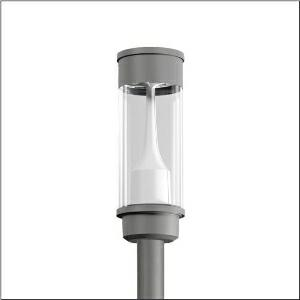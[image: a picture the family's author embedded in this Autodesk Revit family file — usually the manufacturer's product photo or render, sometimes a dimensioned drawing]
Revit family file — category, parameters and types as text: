
# Revit family: litepole_iq___st1_2a_5xa5415af14hp_e371
name_source: partatom
category: Lighting Fixtures
units: mm (PartAtom-declared; Revit-internal decimal feet)

## family parameters
Cut with Voids When Loaded = No
Host = Face
Light Source = No
Part Type = Normal
Room Calculation Point = No
Round Connector Dimension = Use Diameter
Shared = No

## types (1)
- --- (1 x LED, 3910 lm, 33.6 W, 2200K)
    Apparent Load = 34 VA
    CIE Flux Codes = 22 60 93 95 100
    Color Rendering = 70
    Color Temperature = 2200K
    Default Elevation = 1800 mm
    Description = Litepole iQ, mast luminaire, Module 540 iQ-SR, primary light control with 3 zone facetted reflector, of plastic, silver coated, highly specular, structured, primary optical cover: cover, of PMMA, transparent, partly coated, light distribution: ST1.2a, light emission: direct distribution, primary light characteristic: asymmetric, installation type: post-top, LED, High Power LED, rated luminous flux: 3.910lm, luminous efficacy: 116lm/W, light colour: 722, colour temperature: 2200K, control gear: iQ Street-Remote, control: optimised constant luminous flux control (CLO 2.0), Desk-Remote (wireless, voltage-free reading and setting of iQ features in the workshop via application-optimized NFC function/RFID function), Light-Fading, Smart-Wire, Night-Set, Lumen-Switch, Temp-Guard, Auto-Match, Street-Remote, pre-setting: logarithmic dimming characteristic, with terminal, 6-pole, max. 2.5mm², mains connection: 230..240V, AC, 50/60Hz, start of lifetime: 34W, end of service life: 36W, reduction: 15W, luminaire housing, upper part, of glass-fibre reinforced polyester, coated, Siteco® metallic grey (DB 702S), diameter: 210mm, height: 590mm, spigot size: d x l = 76 x 70mm (post-top) | with reducer (optional accessory) 60 x 70mm, mounting height: 3..5m, post-top mast mounting element, of diecast aluminium, coated, Siteco® metallic grey (DB 702S), Module 540 iQ-SR, traffic white (RAL 9016), equipment: Power, protection rating (complete): IP65, insulation class (complete): insulation class II (safety insulation), certification: CE, ENEC, VDE, packaging unit: 1 piece

Light Distribution: ST1.2a
    Height = 590 mm
    Lamp = 1 x LED
    Lamp Light Flux = 3910 lm
    Lamp Power = 33.6 W
    Lamp count = 1
    Length = 220 mm
    Luminous efficacy = 116 lm/W
    Manufacturer = Siteco
    ModVariant = No
    Model = 5XA5415AF14HP
    Number of Poles = 1
    OnlyDefault = Yes
    Power Factor = 1
    Product Name = Litepole iQ | ST1.2a
    Product group = mast luminaire | pylon top
    ProductGroupID = 6100
    Protection Class = Protection class II
    Protection Degree = IP 65
    RLX_Detail_Level = 1
    RLX_Emergency_Light_Flux = 0 lm
    RLX_Emergency_Type = 0
    RLX_Emergency_Type_DB = No
    RlxData = <blob elided: 29725 chars, md5=054f4d41>
    Socket = socket
    Standby Power = 0 W
    System Light Flux = 3910 lm
    System Power = 34 W
    Type Comments = factory setting: luminous flux: 100 % | dim-lin: 254 | 695 mA
    Type Image = l_1006025.jpg
    URL = http://relux.com
    VarID = @adj_216387
    Voltage = 0 V
    Weight = 0.00 kg
    Width = 0 mm  [stored 0 ft]

note: [stored X ft] marks values corroborated as IEEE doubles in the binary element streams (Revit-internal decimal feet)

## geometry (parser evidence)
native form markers: Blend x4, Sweep x9
no freeform markers — native parametric forms only
